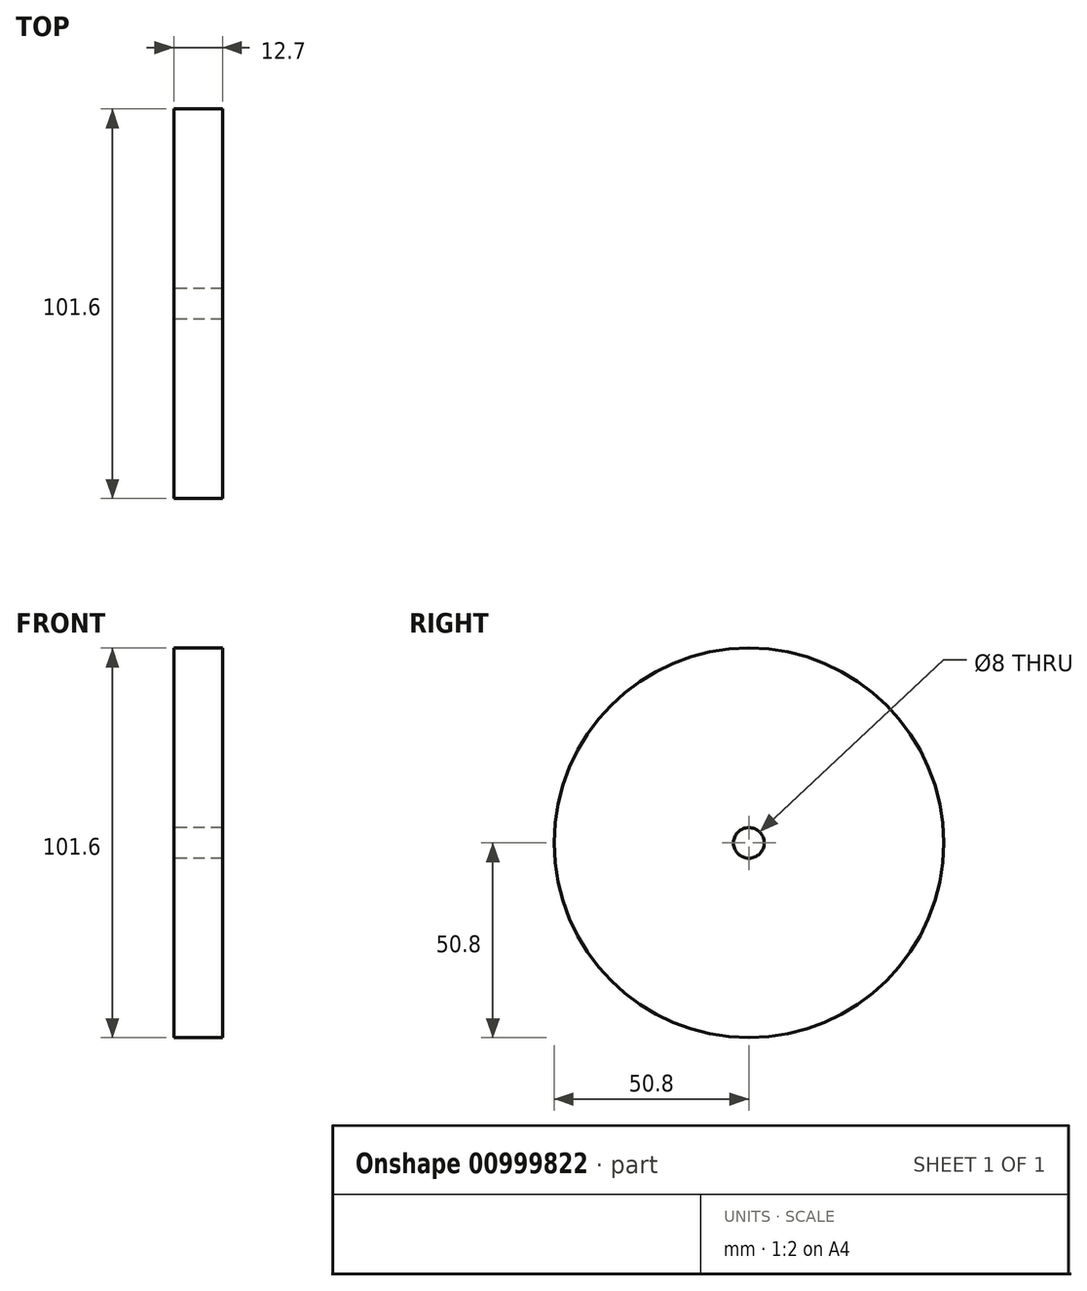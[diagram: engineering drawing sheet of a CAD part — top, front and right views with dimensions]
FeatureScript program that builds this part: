
annotation { "Feature Type Name" : "Feature", "Feature Type Description" : "" }
export const myFeature = defineFeature(function(context is Context, id is Id, definition is map)
    precondition{}
    {
        {
            var Q0;
            Q0=qCreatedBy(makeId("Right.planeOp"),FACE);
            var sketch = newSketch(context, id + "F0", { "sketchPlane" : qUnion([Q0])});
            skCircle(sketch, "E0", {"center": v(0, 0) * mm, "radius": 50.8 * mm});
            skCircle(sketch, "E1", {"center": v(0, 0) * mm, "radius": 4 * mm});
            skSolve(sketch);
        }
        {
            var Q0;
            Q0=makeQuery(id+"F0.imprint","IMPRINT",FACE,{"disambiguationData":[TD([[makeQuery(id+"F0.imprint","IMPRINT",EDGE,{"derivedFrom":sQuery(id+"F0.wireOp",EDGE,"E0")}),1.0]])]});
            extrude(context, id + "F1", {"entities" : qUnion([Q0]), "depth" : 12.7 * mm, "offsetDistance" : 25.4 * mm});
        }
    });
